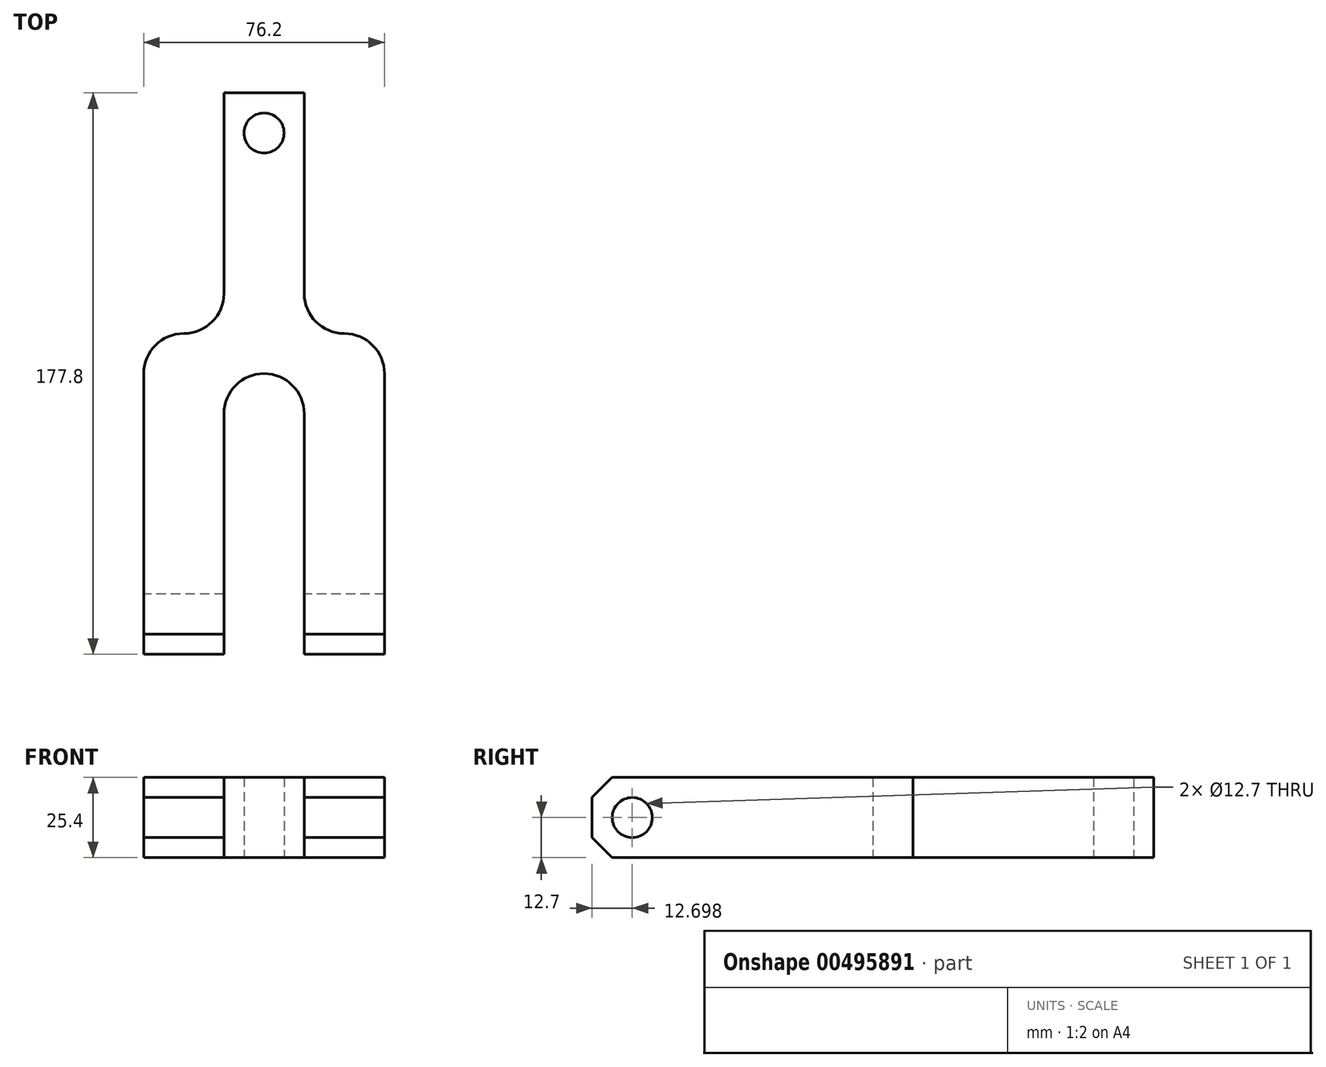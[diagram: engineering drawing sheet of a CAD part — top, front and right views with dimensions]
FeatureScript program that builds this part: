
annotation { "Feature Type Name" : "Feature", "Feature Type Description" : "" }
export const myFeature = defineFeature(function(context is Context, id is Id, definition is map)
    precondition{}
    {
        {
            var Q0;
            Q0=qCreatedBy(makeId("Top.planeOp"),FACE);
            var sketch = newSketch(context, id + "F0", { "sketchPlane" : qUnion([Q0])});
            skLineSegment(sketch, "E0", {"start": v(0, 84.9) * mm, "end": v(25.4, 84.9) * mm});
            skLineSegment(sketch, "E1", {"start": v(0, 84.9) * mm, "end": v(0, 21.4) * mm});
            skLineSegment(sketch, "E2", {"start": v(-12.7, 8.7) * mm, "end": v(-12.7, 8.7) * mm});
            skLineSegment(sketch, "E3", {"start": v(-25.4, -4) * mm, "end": v(-25.4, -92.9) * mm});
            skLineSegment(sketch, "E4", {"start": v(-25.4, -92.9) * mm, "end": v(0, -92.9) * mm});
            skLineSegment(sketch, "E5", {"start": v(25.4, -92.9) * mm, "end": v(50.8, -92.9) * mm});
            skLineSegment(sketch, "E6", {"start": v(50.8, -92.9) * mm, "end": v(50.8, -4) * mm});
            skLineSegment(sketch, "E7", {"start": v(25.4, 84.9) * mm, "end": v(25.4, 21.4) * mm});
            skLineSegment(sketch, "E8", {"start": v(38.1, 8.7) * mm, "end": v(38.1, 8.7) * mm});
            skCircle(sketch, "E9", {"center": v(12.7, 72.2) * mm, "radius": 6.35 * mm});
            skLineSegment(sketch, "E10", {"start": v(0, -92.9) * mm, "end": v(0, -16.7) * mm});
            skLineSegment(sketch, "E11", {"start": v(25.4, -92.9) * mm, "end": v(25.4, -16.7) * mm});
            skArc(sketch, "E12", {"start": v(25.4, -16.7) * mm, "mid": v(12.7, -4) * mm, "end": v(0, -16.7) * mm});
            skPoint(sketch, "E13.visualSharp", {"position": v(0, 8.7) * mm});
            skArc(sketch, "E13.filletArc", {"start": v(-12.7, 8.7) * mm, "mid": v(-3.72, 12.43) * mm, "end": v(0, 21.4) * mm});
            skPoint(sketch, "E14.visualSharp", {"position": v(25.4, 8.7) * mm});
            skArc(sketch, "E14.filletArc", {"start": v(25.4, 21.4) * mm, "mid": v(29.12, 12.43) * mm, "end": v(38.1, 8.7) * mm});
            skPoint(sketch, "E15.visualSharp", {"position": v(50.8, 8.7) * mm});
            skArc(sketch, "E15.filletArc", {"start": v(50.8, -4) * mm, "mid": v(47.08, 4.99) * mm, "end": v(38.1, 8.7) * mm});
            skPoint(sketch, "E16.visualSharp", {"position": v(-25.4, 8.7) * mm});
            skArc(sketch, "E16.filletArc", {"start": v(-12.7, 8.7) * mm, "mid": v(-21.68, 4.99) * mm, "end": v(-25.4, -4) * mm});
            skSolve(sketch);
        }
        {
            var Q0;
            Q0=makeQuery(id+"F0.imprint","IMPRINT",FACE,{"disambiguationData":[TD([[makeQuery(id+"F0.imprint","IMPRINT",EDGE,{"derivedFrom":sQuery(id+"F0.wireOp",EDGE,"E0")}),-1.0]])]});
            extrude(context, id + "F1", {"entities" : qUnion([Q0]), "depth" : 25.4 * mm});
        }
        {
            var Q0;
            Q0=makeQuery(id+"F1.opExtrude","SWEPT_FACE",FACE,{"disambiguationData":[OSD([sQuery(id+"F0.wireOp",EDGE,"E3")])]});
            var sketch = newSketch(context, id + "F2", { "sketchPlane" : qUnion([Q0])});
            skCircle(sketch, "E17", {"center": v(80.2, 12.7) * mm, "radius": 6.35 * mm});
            skPoint(sketch, "E17.centerSnap0", {"position": v(92.9, 12.7) * mm});
            skSolve(sketch);
        }
        {
            var Q0;
            Q0=makeQuery(id+"F2.imprint","IMPRINT",FACE,{"disambiguationData":[TD([[makeQuery(id+"F2.imprint","IMPRINT",EDGE,{"derivedFrom":sQuery(id+"F2.wireOp",EDGE,"E17")}),1.0]])]});
            extrude(context, id + "F3", {"entities" : qUnion([Q0]), "operationType" : NewBodyOperationType.REMOVE, "oppositeDirection" : true, "depth" : 76.2 * mm});
        }
        {
            var Q0;
            Q0=makeQuery(id+"F1.opExtrude","CAP_EDGE",EDGE,{"disambiguationData":[OSD([sQuery(id+"F0.wireOp",EDGE,"E4")])],"isStart":false});
            var Q1;
            Q1=makeQuery(id+"F1.opExtrude","CAP_EDGE",EDGE,{"disambiguationData":[OSD([sQuery(id+"F0.wireOp",EDGE,"E4")])],"isStart":true});
            var Q2;
            Q2=makeQuery(id+"F1.opExtrude","CAP_EDGE",EDGE,{"disambiguationData":[OSD([sQuery(id+"F0.wireOp",EDGE,"E5")])],"isStart":false});
            var Q3;
            Q3=makeQuery(id+"F1.opExtrude","CAP_EDGE",EDGE,{"disambiguationData":[OSD([sQuery(id+"F0.wireOp",EDGE,"E5")])],"isStart":true});
            chamfer(context, id + "F4", {"entities" : qUnion([Q0, Q1, Q2, Q3]), "width" : 6.35 * mm, "tangentPropagation" : true});
        }
    });
